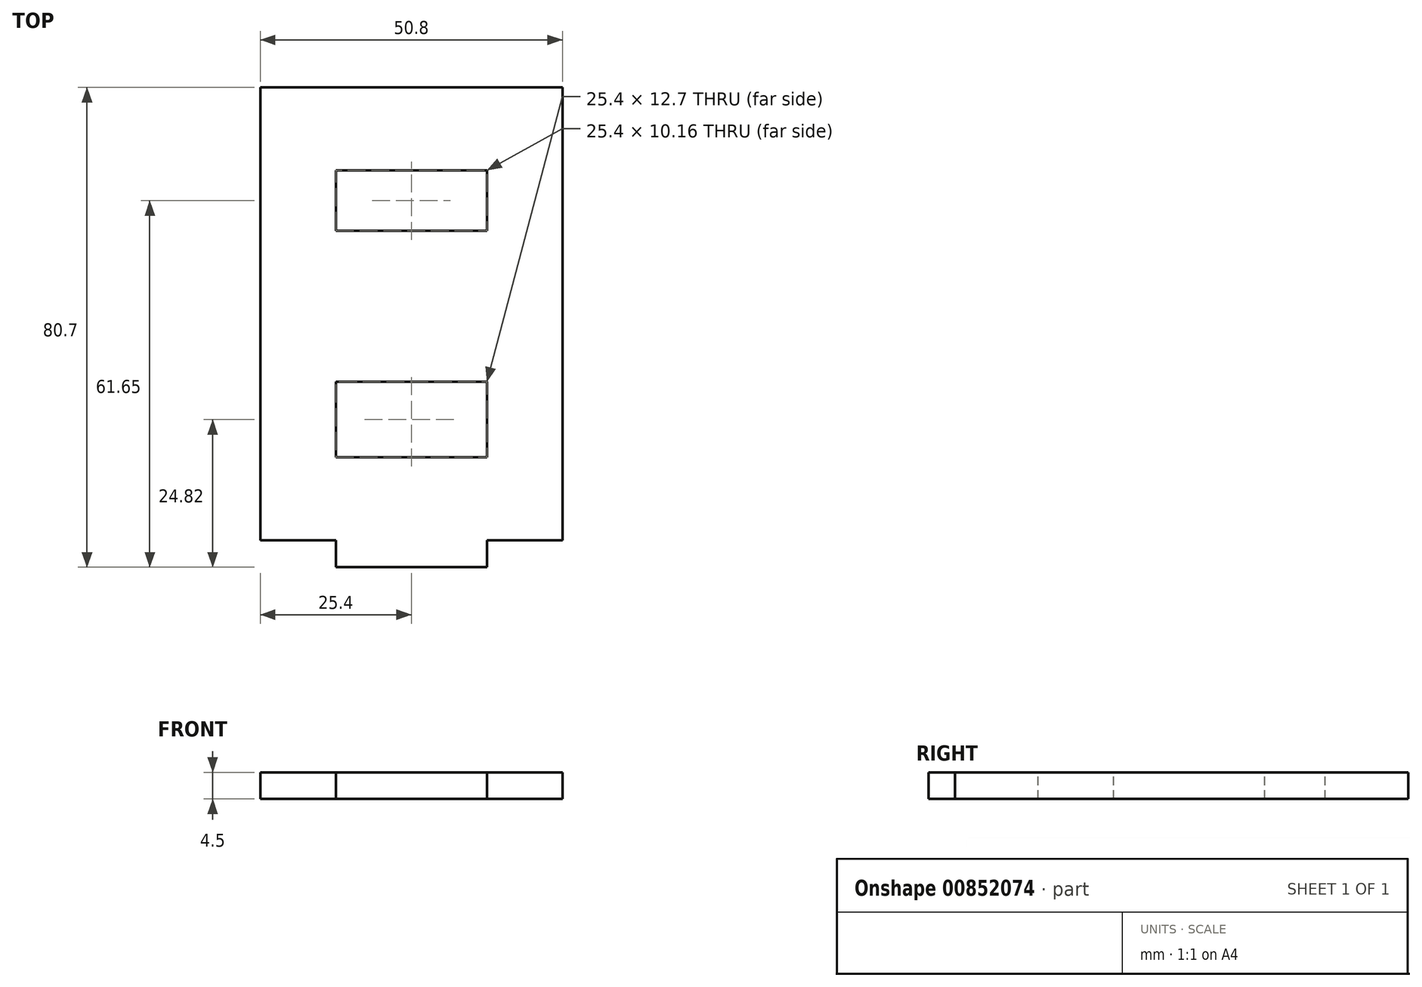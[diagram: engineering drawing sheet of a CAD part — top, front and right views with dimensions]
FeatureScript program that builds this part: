
annotation { "Feature Type Name" : "Feature", "Feature Type Description" : "" }
export const myFeature = defineFeature(function(context is Context, id is Id, definition is map)
    precondition{}
    {
        {
            var Q0;
            Q0=qCreatedBy(makeId("Top.planeOp"),FACE);
            var sketch = newSketch(context, id + "F0", { "sketchPlane" : qUnion([Q0])});
            skLineSegment(sketch, "E0.bottom", {"start": v(-25.4, 38.1) * mm, "end": v(25.4, 38.1) * mm});
            skLineSegment(sketch, "E0.top", {"start": v(-25.4, -38.1) * mm, "end": v(-12.7, -38.1) * mm});
            skLineSegment(sketch, "E0.left", {"start": v(-25.4, 38.1) * mm, "end": v(-25.4, -38.1) * mm});
            skLineSegment(sketch, "E0.right", {"start": v(25.4, 38.1) * mm, "end": v(25.4, -38.1) * mm});
            skLineSegment(sketch, "E1", {"start": v(0, 38.1) * mm, "end": v(0, 0) * mm, "construction": true});
            skLineSegment(sketch, "E2", {"start": v(0, 0) * mm, "end": v(-25.4, 0) * mm, "construction": true});
            skLineSegment(sketch, "E3", {"start": v(-12.7, -38.1) * mm, "end": v(-12.7, -42.6) * mm});
            skLineSegment(sketch, "E4", {"start": v(-12.7, -42.6) * mm, "end": v(12.7, -42.6) * mm});
            skLineSegment(sketch, "E5", {"start": v(12.7, -42.6) * mm, "end": v(12.7, -38.1) * mm});
            skLineSegment(sketch, "E6", {"start": v(-12.7, -38.1) * mm, "end": v(12.7, -38.1) * mm, "construction": true});
            skLineSegment(sketch, "E7", {"start": v(12.7, -38.1) * mm, "end": v(25.4, -38.1) * mm});
            skSolve(sketch);
        }
        {
            var Q0;
            Q0 = qSketchRegion(id + "F0", true);
            extrude(context, id + "F1", {"entities" : qUnion([Q0]), "depth" : 4.5 * mm, "offsetDistance" : 25.4 * mm});
        }
        {
            var Q0;
            Q0=makeQuery(id+"F1.opExtrude","CAP_FACE",FACE,{"disambiguationData":[OSD([sQuery(id+"F0.wireOp",EDGE,"E0.bottom"),sQuery(id+"F0.wireOp",EDGE,"E0.top"),sQuery(id+"F0.wireOp",EDGE,"E0.left"),sQuery(id+"F0.wireOp",EDGE,"E0.right"),sQuery(id+"F0.wireOp",EDGE,"E3"),sQuery(id+"F0.wireOp",EDGE,"E4"),sQuery(id+"F0.wireOp",EDGE,"E5"),sQuery(id+"F0.wireOp",EDGE,"E7")])],"isStart":false});
            var sketch = newSketch(context, id + "F2", { "sketchPlane" : qUnion([Q0])});
            skLineSegment(sketch, "E8.bottom", {"start": v(-12.7, 24.13) * mm, "end": v(12.7, 24.13) * mm});
            skLineSegment(sketch, "E8.top", {"start": v(-12.7, 13.97) * mm, "end": v(12.7, 13.97) * mm});
            skLineSegment(sketch, "E8.left", {"start": v(-12.7, 24.13) * mm, "end": v(-12.7, 13.97) * mm});
            skLineSegment(sketch, "E8.right", {"start": v(12.7, 24.13) * mm, "end": v(12.7, 13.97) * mm});
            skLineSegment(sketch, "E9", {"start": v(-12.7, 13.97) * mm, "end": v(0, 38.1) * mm, "construction": true});
            skLineSegment(sketch, "E10", {"start": v(0, 38.1) * mm, "end": v(12.7, 13.97) * mm, "construction": true});
            skLineSegment(sketch, "E11.bottom", {"start": v(-12.7, -11.43) * mm, "end": v(12.7, -11.43) * mm});
            skLineSegment(sketch, "E11.top", {"start": v(-12.7, -24.13) * mm, "end": v(12.7, -24.13) * mm});
            skLineSegment(sketch, "E11.left", {"start": v(-12.7, -11.43) * mm, "end": v(-12.7, -24.13) * mm});
            skLineSegment(sketch, "E11.right", {"start": v(12.7, -11.43) * mm, "end": v(12.7, -24.13) * mm});
            skLineSegment(sketch, "E12", {"start": v(-12.7, 13.97) * mm, "end": v(-12.7, -11.43) * mm, "construction": true});
            skLineSegment(sketch, "E13", {"start": v(12.7, -11.43) * mm, "end": v(12.7, 13.97) * mm, "construction": true});
            skSolve(sketch);
        }
        {
            var Q0;
            Q0 = qSketchRegion(id + "F2", true);
            extrude(context, id + "F3", {"entities" : qUnion([Q0]), "operationType" : NewBodyOperationType.REMOVE, "endBound" : BoundingType.THROUGH_ALL, "oppositeDirection" : true, "depth" : 25.4 * mm, "offsetDistance" : 25.4 * mm});
        }
    });
